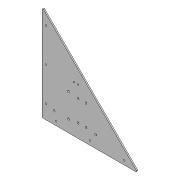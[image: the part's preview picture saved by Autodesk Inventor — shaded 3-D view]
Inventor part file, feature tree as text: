
AUTODESK INVENTOR PART (.ipt)
format: ipt  version: 2020 (Build 240168000, 168)  size: 163,840 bytes
history: native  units: mm
features: sketch x5, hole x4, other x2, projected_geometry x2, fillet x1
ambient origin geometry x8: Origin, YZ Plane, XZ Plane, XY Plane, X Axis, Y Axis, Z Axis, Center Point
bodies: Body1 (feature_tree)
feature tree (14):
  other  "ソリッド1"
  hole  "穴1"  [1 undecoded]
  fillet  "フィレット1"  Radius=20.0mm
  hole  "穴2"  [1 undecoded]
  hole  "穴3"  [1 undecoded]
  hole  "穴4"  [1 undecoded]
  sketch  "スケッチ1"
  other  "プレート1"
  sketch  "スケッチ2"
  sketch  "スケッチ3"
  sketch  "スケッチ4"
  projected_geometry  "投影ループ1"
  sketch  "スケッチ6"
  projected_geometry  "投影ループ3"
note: 4 required parameter values undecoded (feature->parameter linkage not recoverable at this tier; creation-order binding heuristic only, values carry confidence <= 0.55)
